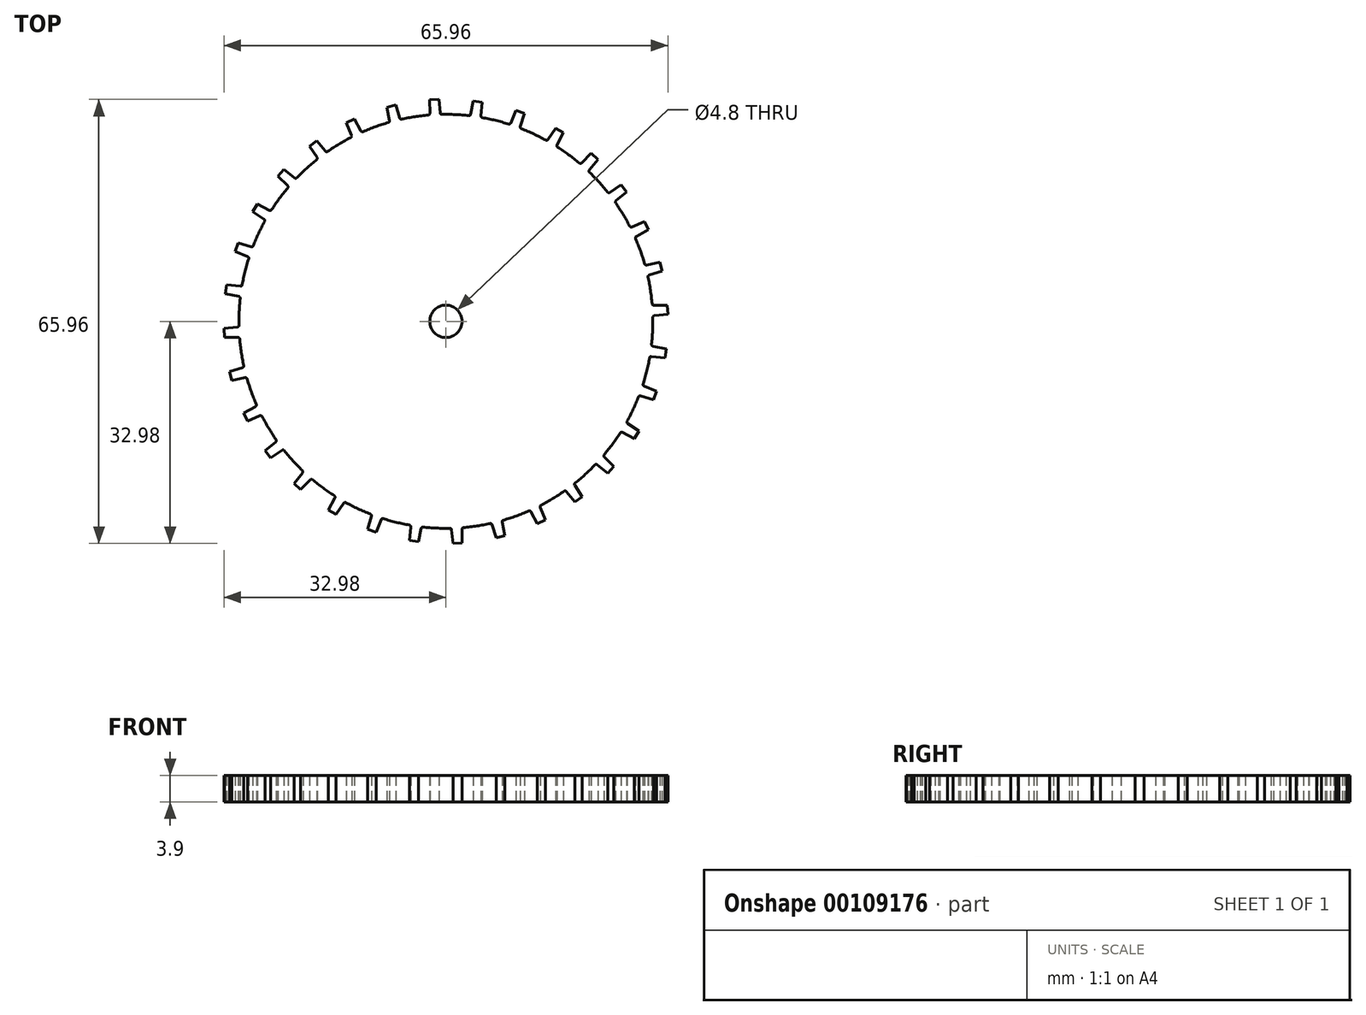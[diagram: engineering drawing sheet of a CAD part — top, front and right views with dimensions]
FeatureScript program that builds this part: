
annotation { "Feature Type Name" : "Feature", "Feature Type Description" : "" }
export const myFeature = defineFeature(function(context is Context, id is Id, definition is map)
    precondition{}
    {
        {
            var Q0;
            Q0=qCreatedBy(makeId("Top.planeOp"),FACE);
            var sketch = newSketch(context, id + "F0", { "sketchPlane" : qUnion([Q0])});
            skCircle(sketch, "E0", {"center": v(0, 0) * mm, "radius": 2.4 * mm});
            skCircle(sketch, "E1", {"center": v(0, 0) * mm, "radius": 32 * mm, "construction": true});
            skCircle(sketch, "E2", {"center": v(0, 0) * mm, "radius": 30.75 * mm});
            skCircle(sketch, "E3", {"center": v(0, 0) * mm, "radius": 31 * mm, "construction": true});
            skCircle(sketch, "E4", {"center": v(0, 0) * mm, "radius": 33 * mm, "construction": true});
            skLineSegment(sketch, "E5", {"start": v(3.64, 30.53) * mm, "end": v(4.08, 32.75) * mm});
            skLineSegment(sketch, "E6", {"start": v(5.4, 32.55) * mm, "end": v(5.2, 30.3) * mm});
            skLineSegment(sketch, "E7", {"start": v(4.08, 32.75) * mm, "end": v(5.4, 32.55) * mm});
            skLineSegment(sketch, "E8.1.0", {"start": v(10.39, 31.32) * mm, "end": v(11.65, 30.87) * mm});
            skLineSegment(sketch, "E8.1.1", {"start": v(11.65, 30.87) * mm, "end": v(11, 28.71) * mm});
            skLineSegment(sketch, "E8.1.2", {"start": v(9.53, 29.24) * mm, "end": v(10.39, 31.32) * mm});
            skLineSegment(sketch, "E8.2.0", {"start": v(16.3, 28.7) * mm, "end": v(17.45, 28) * mm});
            skLineSegment(sketch, "E8.2.1", {"start": v(17.45, 28) * mm, "end": v(16.4, 26.02) * mm});
            skLineSegment(sketch, "E8.2.2", {"start": v(15.05, 26.82) * mm, "end": v(16.3, 28.7) * mm});
            skLineSegment(sketch, "E8.3.0", {"start": v(21.58, 24.96) * mm, "end": v(22.58, 24.07) * mm});
            skLineSegment(sketch, "E8.3.1", {"start": v(22.58, 24.07) * mm, "end": v(21.15, 22.32) * mm});
            skLineSegment(sketch, "E8.3.2", {"start": v(20, 23.36) * mm, "end": v(21.58, 24.96) * mm});
            skLineSegment(sketch, "E8.4.0", {"start": v(26.04, 20.27) * mm, "end": v(26.84, 19.2) * mm});
            skLineSegment(sketch, "E8.4.1", {"start": v(26.84, 19.2) * mm, "end": v(25.1, 17.76) * mm});
            skLineSegment(sketch, "E8.4.2", {"start": v(24.17, 19.02) * mm, "end": v(26.04, 20.27) * mm});
            skLineSegment(sketch, "E8.5.0", {"start": v(29.5, 14.8) * mm, "end": v(30.07, 13.6) * mm});
            skLineSegment(sketch, "E8.5.1", {"start": v(30.07, 13.6) * mm, "end": v(28.08, 12.52) * mm});
            skLineSegment(sketch, "E8.5.2", {"start": v(27.41, 13.94) * mm, "end": v(29.5, 14.8) * mm});
            skLineSegment(sketch, "E8.6.0", {"start": v(31.81, 8.77) * mm, "end": v(32.14, 7.46) * mm});
            skLineSegment(sketch, "E8.6.1", {"start": v(32.14, 7.46) * mm, "end": v(29.99, 6.8) * mm});
            skLineSegment(sketch, "E8.6.2", {"start": v(29.6, 8.32) * mm, "end": v(31.81, 8.77) * mm});
            skLineSegment(sketch, "E8.7.0", {"start": v(32.91, 2.4) * mm, "end": v(32.98, 1.05) * mm});
            skLineSegment(sketch, "E8.7.1", {"start": v(32.98, 1.05) * mm, "end": v(30.74, 0.82) * mm});
            skLineSegment(sketch, "E8.7.2", {"start": v(30.66, 2.38) * mm, "end": v(32.91, 2.4) * mm});
            skLineSegment(sketch, "E8.8.0", {"start": v(32.75, -4.08) * mm, "end": v(32.55, -5.4) * mm});
            skLineSegment(sketch, "E8.8.1", {"start": v(32.55, -5.4) * mm, "end": v(30.3, -5.2) * mm});
            skLineSegment(sketch, "E8.8.2", {"start": v(30.53, -3.64) * mm, "end": v(32.75, -4.08) * mm});
            skLineSegment(sketch, "E8.9.0", {"start": v(31.32, -10.39) * mm, "end": v(30.87, -11.65) * mm});
            skLineSegment(sketch, "E8.9.1", {"start": v(30.87, -11.65) * mm, "end": v(28.71, -11) * mm});
            skLineSegment(sketch, "E8.9.2", {"start": v(29.24, -9.53) * mm, "end": v(31.32, -10.39) * mm});
            skLineSegment(sketch, "E8.10.0", {"start": v(28.7, -16.3) * mm, "end": v(28, -17.45) * mm});
            skLineSegment(sketch, "E8.10.1", {"start": v(28, -17.45) * mm, "end": v(26.02, -16.4) * mm});
            skLineSegment(sketch, "E8.10.2", {"start": v(26.82, -15.05) * mm, "end": v(28.7, -16.3) * mm});
            skLineSegment(sketch, "E8.11.0", {"start": v(24.96, -21.58) * mm, "end": v(24.07, -22.58) * mm});
            skLineSegment(sketch, "E8.11.1", {"start": v(24.07, -22.58) * mm, "end": v(22.32, -21.15) * mm});
            skLineSegment(sketch, "E8.11.2", {"start": v(23.36, -20) * mm, "end": v(24.96, -21.58) * mm});
            skLineSegment(sketch, "E8.12.0", {"start": v(20.27, -26.04) * mm, "end": v(19.2, -26.84) * mm});
            skLineSegment(sketch, "E8.12.1", {"start": v(19.2, -26.84) * mm, "end": v(17.76, -25.1) * mm});
            skLineSegment(sketch, "E8.12.2", {"start": v(19.02, -24.17) * mm, "end": v(20.27, -26.04) * mm});
            skLineSegment(sketch, "E8.13.0", {"start": v(14.8, -29.5) * mm, "end": v(13.6, -30.07) * mm});
            skLineSegment(sketch, "E8.13.1", {"start": v(13.6, -30.07) * mm, "end": v(12.52, -28.08) * mm});
            skLineSegment(sketch, "E8.13.2", {"start": v(13.94, -27.41) * mm, "end": v(14.8, -29.5) * mm});
            skLineSegment(sketch, "E8.14.0", {"start": v(8.77, -31.81) * mm, "end": v(7.46, -32.14) * mm});
            skLineSegment(sketch, "E8.14.1", {"start": v(7.46, -32.14) * mm, "end": v(6.8, -29.99) * mm});
            skLineSegment(sketch, "E8.14.2", {"start": v(8.32, -29.6) * mm, "end": v(8.77, -31.81) * mm});
            skLineSegment(sketch, "E8.15.0", {"start": v(2.4, -32.91) * mm, "end": v(1.05, -32.98) * mm});
            skLineSegment(sketch, "E8.15.1", {"start": v(1.05, -32.98) * mm, "end": v(0.82, -30.74) * mm});
            skLineSegment(sketch, "E8.15.2", {"start": v(2.38, -30.66) * mm, "end": v(2.4, -32.91) * mm});
            skLineSegment(sketch, "E8.16.0", {"start": v(-4.08, -32.75) * mm, "end": v(-5.4, -32.55) * mm});
            skLineSegment(sketch, "E8.16.1", {"start": v(-5.4, -32.55) * mm, "end": v(-5.2, -30.3) * mm});
            skLineSegment(sketch, "E8.16.2", {"start": v(-3.64, -30.53) * mm, "end": v(-4.08, -32.75) * mm});
            skLineSegment(sketch, "E8.17.0", {"start": v(-10.39, -31.32) * mm, "end": v(-11.65, -30.87) * mm});
            skLineSegment(sketch, "E8.17.1", {"start": v(-11.65, -30.87) * mm, "end": v(-11, -28.71) * mm});
            skLineSegment(sketch, "E8.17.2", {"start": v(-9.53, -29.24) * mm, "end": v(-10.39, -31.32) * mm});
            skLineSegment(sketch, "E8.18.0", {"start": v(-16.3, -28.7) * mm, "end": v(-17.45, -28) * mm});
            skLineSegment(sketch, "E8.18.1", {"start": v(-17.45, -28) * mm, "end": v(-16.4, -26.02) * mm});
            skLineSegment(sketch, "E8.18.2", {"start": v(-15.05, -26.82) * mm, "end": v(-16.3, -28.7) * mm});
            skLineSegment(sketch, "E8.19.0", {"start": v(-21.58, -24.96) * mm, "end": v(-22.58, -24.07) * mm});
            skLineSegment(sketch, "E8.19.1", {"start": v(-22.58, -24.07) * mm, "end": v(-21.15, -22.32) * mm});
            skLineSegment(sketch, "E8.19.2", {"start": v(-20, -23.36) * mm, "end": v(-21.58, -24.96) * mm});
            skLineSegment(sketch, "E8.20.0", {"start": v(-26.04, -20.27) * mm, "end": v(-26.84, -19.2) * mm});
            skLineSegment(sketch, "E8.20.1", {"start": v(-26.84, -19.2) * mm, "end": v(-25.1, -17.76) * mm});
            skLineSegment(sketch, "E8.20.2", {"start": v(-24.17, -19.02) * mm, "end": v(-26.04, -20.27) * mm});
            skLineSegment(sketch, "E8.21.0", {"start": v(-29.5, -14.8) * mm, "end": v(-30.07, -13.6) * mm});
            skLineSegment(sketch, "E8.21.1", {"start": v(-30.07, -13.6) * mm, "end": v(-28.08, -12.52) * mm});
            skLineSegment(sketch, "E8.21.2", {"start": v(-27.41, -13.94) * mm, "end": v(-29.5, -14.8) * mm});
            skLineSegment(sketch, "E8.22.0", {"start": v(-31.81, -8.77) * mm, "end": v(-32.14, -7.46) * mm});
            skLineSegment(sketch, "E8.22.1", {"start": v(-32.14, -7.46) * mm, "end": v(-29.99, -6.8) * mm});
            skLineSegment(sketch, "E8.22.2", {"start": v(-29.6, -8.32) * mm, "end": v(-31.81, -8.77) * mm});
            skLineSegment(sketch, "E8.23.0", {"start": v(-32.91, -2.4) * mm, "end": v(-32.98, -1.05) * mm});
            skLineSegment(sketch, "E8.23.1", {"start": v(-32.98, -1.05) * mm, "end": v(-30.74, -0.82) * mm});
            skLineSegment(sketch, "E8.23.2", {"start": v(-30.66, -2.38) * mm, "end": v(-32.91, -2.4) * mm});
            skLineSegment(sketch, "E8.24.0", {"start": v(-32.75, 4.08) * mm, "end": v(-32.55, 5.4) * mm});
            skLineSegment(sketch, "E8.24.1", {"start": v(-32.55, 5.4) * mm, "end": v(-30.3, 5.2) * mm});
            skLineSegment(sketch, "E8.24.2", {"start": v(-30.53, 3.64) * mm, "end": v(-32.75, 4.08) * mm});
            skLineSegment(sketch, "E8.25.0", {"start": v(-31.32, 10.39) * mm, "end": v(-30.87, 11.65) * mm});
            skLineSegment(sketch, "E8.25.1", {"start": v(-30.87, 11.65) * mm, "end": v(-28.71, 11) * mm});
            skLineSegment(sketch, "E8.25.2", {"start": v(-29.24, 9.53) * mm, "end": v(-31.32, 10.39) * mm});
            skLineSegment(sketch, "E8.26.0", {"start": v(-28.7, 16.3) * mm, "end": v(-28, 17.45) * mm});
            skLineSegment(sketch, "E8.26.1", {"start": v(-28, 17.45) * mm, "end": v(-26.02, 16.4) * mm});
            skLineSegment(sketch, "E8.26.2", {"start": v(-26.82, 15.05) * mm, "end": v(-28.7, 16.3) * mm});
            skLineSegment(sketch, "E8.27.0", {"start": v(-24.96, 21.58) * mm, "end": v(-24.07, 22.58) * mm});
            skLineSegment(sketch, "E8.27.1", {"start": v(-24.07, 22.58) * mm, "end": v(-22.32, 21.15) * mm});
            skLineSegment(sketch, "E8.27.2", {"start": v(-23.36, 20) * mm, "end": v(-24.96, 21.58) * mm});
            skLineSegment(sketch, "E8.28.0", {"start": v(-20.27, 26.04) * mm, "end": v(-19.2, 26.84) * mm});
            skLineSegment(sketch, "E8.28.1", {"start": v(-19.2, 26.84) * mm, "end": v(-17.76, 25.1) * mm});
            skLineSegment(sketch, "E8.28.2", {"start": v(-19.02, 24.17) * mm, "end": v(-20.27, 26.04) * mm});
            skLineSegment(sketch, "E8.29.0", {"start": v(-14.8, 29.5) * mm, "end": v(-13.6, 30.07) * mm});
            skLineSegment(sketch, "E8.29.1", {"start": v(-13.6, 30.07) * mm, "end": v(-12.52, 28.08) * mm});
            skLineSegment(sketch, "E8.29.2", {"start": v(-13.94, 27.41) * mm, "end": v(-14.8, 29.5) * mm});
            skLineSegment(sketch, "E8.30.0", {"start": v(-8.77, 31.81) * mm, "end": v(-7.46, 32.14) * mm});
            skLineSegment(sketch, "E8.30.1", {"start": v(-7.46, 32.14) * mm, "end": v(-6.8, 29.99) * mm});
            skLineSegment(sketch, "E8.30.2", {"start": v(-8.32, 29.6) * mm, "end": v(-8.77, 31.81) * mm});
            skLineSegment(sketch, "E8.31.0", {"start": v(-2.4, 32.91) * mm, "end": v(-1.05, 32.98) * mm});
            skLineSegment(sketch, "E8.31.1", {"start": v(-1.05, 32.98) * mm, "end": v(-0.82, 30.74) * mm});
            skLineSegment(sketch, "E8.31.2", {"start": v(-2.38, 30.66) * mm, "end": v(-2.4, 32.91) * mm});
            skLineSegment(sketch, "E8.anchor1", {"start": v(0, 0) * mm, "end": v(4.08, 32.75) * mm, "construction": true});
            skLineSegment(sketch, "E8.anchor2", {"start": v(0, 0) * mm, "end": v(-2.4, 32.91) * mm, "construction": true});
            skSolve(sketch);
        }
        {
            var Q0;
            Q0=makeQuery(id+"F0.imprint","IMPRINT",FACE,{"disambiguationData":[TD([[makeQuery(id+"F0.imprint","IMPRINT",EDGE,{"derivedFrom":sQuery(id+"F0.wireOp",EDGE,"E8.14.0")}),-1.0]])]});
            var Q1;
            Q1=makeQuery(id+"F0.imprint","IMPRINT",FACE,{"disambiguationData":[TD([[makeQuery(id+"F0.imprint","IMPRINT",EDGE,{"derivedFrom":sQuery(id+"F0.wireOp",EDGE,"E8.11.0")}),-1.0]])]});
            var Q2;
            Q2=makeQuery(id+"F0.imprint","IMPRINT",FACE,{"disambiguationData":[TD([[makeQuery(id+"F0.imprint","IMPRINT",EDGE,{"derivedFrom":sQuery(id+"F0.wireOp",EDGE,"E8.13.0")}),-1.0]])]});
            var Q3;
            Q3=makeQuery(id+"F0.imprint","IMPRINT",FACE,{"disambiguationData":[TD([[makeQuery(id+"F0.imprint","IMPRINT",EDGE,{"derivedFrom":sQuery(id+"F0.wireOp",EDGE,"E8.10.0")}),-1.0]])]});
            var Q4;
            Q4=makeQuery(id+"F0.imprint","IMPRINT",FACE,{"disambiguationData":[TD([[makeQuery(id+"F0.imprint","IMPRINT",EDGE,{"derivedFrom":sQuery(id+"F0.wireOp",EDGE,"E8.12.0")}),-1.0]])]});
            var Q5;
            Q5=makeQuery(id+"F0.imprint","IMPRINT",FACE,{"disambiguationData":[TD([[makeQuery(id+"F0.imprint","IMPRINT",EDGE,{"derivedFrom":sQuery(id+"F0.wireOp",EDGE,"E8.18.0")}),-1.0]])]});
            var Q6;
            Q6=makeQuery(id+"F0.imprint","IMPRINT",FACE,{"disambiguationData":[TD([[makeQuery(id+"F0.imprint","IMPRINT",EDGE,{"derivedFrom":sQuery(id+"F0.wireOp",EDGE,"E8.8.0")}),-1.0]])]});
            var Q7;
            Q7=makeQuery(id+"F0.imprint","IMPRINT",FACE,{"disambiguationData":[TD([[makeQuery(id+"F0.imprint","IMPRINT",EDGE,{"derivedFrom":sQuery(id+"F0.wireOp",EDGE,"E8.7.0")}),-1.0]])]});
            var Q8;
            Q8=makeQuery(id+"F0.imprint","IMPRINT",FACE,{"disambiguationData":[TD([[makeQuery(id+"F0.imprint","IMPRINT",EDGE,{"derivedFrom":sQuery(id+"F0.wireOp",EDGE,"E8.6.0")}),-1.0]])]});
            var Q9;
            Q9=makeQuery(id+"F0.imprint","IMPRINT",FACE,{"disambiguationData":[TD([[makeQuery(id+"F0.imprint","IMPRINT",EDGE,{"derivedFrom":sQuery(id+"F0.wireOp",EDGE,"E8.5.0")}),-1.0]])]});
            var Q10;
            Q10=makeQuery(id+"F0.imprint","IMPRINT",FACE,{"disambiguationData":[TD([[makeQuery(id+"F0.imprint","IMPRINT",EDGE,{"derivedFrom":sQuery(id+"F0.wireOp",EDGE,"E8.4.0")}),-1.0]])]});
            var Q11;
            Q11=makeQuery(id+"F0.imprint","IMPRINT",FACE,{"disambiguationData":[TD([[makeQuery(id+"F0.imprint","IMPRINT",EDGE,{"derivedFrom":sQuery(id+"F0.wireOp",EDGE,"E8.3.0")}),-1.0]])]});
            var Q12;
            Q12=makeQuery(id+"F0.imprint","IMPRINT",FACE,{"disambiguationData":[TD([[makeQuery(id+"F0.imprint","IMPRINT",EDGE,{"derivedFrom":sQuery(id+"F0.wireOp",EDGE,"E8.2.0")}),-1.0]])]});
            var Q13;
            Q13=makeQuery(id+"F0.imprint","IMPRINT",FACE,{"disambiguationData":[TD([[makeQuery(id+"F0.imprint","IMPRINT",EDGE,{"derivedFrom":sQuery(id+"F0.wireOp",EDGE,"E8.1.0")}),-1.0]])]});
            var Q14;
            {var subQ0=sQuery(id+"F0.wireOp",EDGE,"E5");Q14=makeQuery(id+"F0.imprint","IMPRINT",FACE,{"disambiguationData":[TD([[makeQuery(id+"F0.imprint","IMPRINT",EDGE,{"derivedFrom":subQ0}),-1.0]])]});}
            var Q15;
            Q15=makeQuery(id+"F0.imprint","IMPRINT",FACE,{"disambiguationData":[TD([[makeQuery(id+"F0.imprint","IMPRINT",EDGE,{"derivedFrom":sQuery(id+"F0.wireOp",EDGE,"E8.31.0")}),-1.0]])]});
            var Q16;
            Q16=makeQuery(id+"F0.imprint","IMPRINT",FACE,{"disambiguationData":[TD([[makeQuery(id+"F0.imprint","IMPRINT",EDGE,{"derivedFrom":sQuery(id+"F0.wireOp",EDGE,"E8.30.0")}),-1.0]])]});
            var Q17;
            Q17=makeQuery(id+"F0.imprint","IMPRINT",FACE,{"disambiguationData":[TD([[makeQuery(id+"F0.imprint","IMPRINT",EDGE,{"derivedFrom":sQuery(id+"F0.wireOp",EDGE,"E8.29.0")}),-1.0]])]});
            var Q18;
            Q18=makeQuery(id+"F0.imprint","IMPRINT",FACE,{"disambiguationData":[TD([[makeQuery(id+"F0.imprint","IMPRINT",EDGE,{"derivedFrom":sQuery(id+"F0.wireOp",EDGE,"E8.17.0")}),-1.0]])]});
            var Q19;
            Q19=makeQuery(id+"F0.imprint","IMPRINT",FACE,{"disambiguationData":[TD([[makeQuery(id+"F0.imprint","IMPRINT",EDGE,{"derivedFrom":sQuery(id+"F0.wireOp",EDGE,"E8.16.0")}),-1.0]])]});
            var Q20;
            Q20=makeQuery(id+"F0.imprint","IMPRINT",FACE,{"disambiguationData":[TD([[makeQuery(id+"F0.imprint","IMPRINT",EDGE,{"derivedFrom":sQuery(id+"F0.wireOp",EDGE,"E8.9.0")}),-1.0]])]});
            var Q21;
            Q21=makeQuery(id+"F0.imprint","IMPRINT",FACE,{"disambiguationData":[TD([[makeQuery(id+"F0.imprint","IMPRINT",EDGE,{"derivedFrom":sQuery(id+"F0.wireOp",EDGE,"E8.15.0")}),-1.0]])]});
            var Q22;
            Q22=makeQuery(id+"F0.imprint","IMPRINT",FACE,{"disambiguationData":[TD([[makeQuery(id+"F0.imprint","IMPRINT",EDGE,{"derivedFrom":sQuery(id+"F0.wireOp",EDGE,"E0")}),-1.0]])]});
            var Q23;
            Q23=makeQuery(id+"F0.imprint","IMPRINT",FACE,{"disambiguationData":[TD([[makeQuery(id+"F0.imprint","IMPRINT",EDGE,{"derivedFrom":sQuery(id+"F0.wireOp",EDGE,"E8.21.0")}),-1.0]])]});
            var Q24;
            Q24=makeQuery(id+"F0.imprint","IMPRINT",FACE,{"disambiguationData":[TD([[makeQuery(id+"F0.imprint","IMPRINT",EDGE,{"derivedFrom":sQuery(id+"F0.wireOp",EDGE,"E8.20.0")}),-1.0]])]});
            var Q25;
            Q25=makeQuery(id+"F0.imprint","IMPRINT",FACE,{"disambiguationData":[TD([[makeQuery(id+"F0.imprint","IMPRINT",EDGE,{"derivedFrom":sQuery(id+"F0.wireOp",EDGE,"E8.25.0")}),-1.0]])]});
            var Q26;
            Q26=makeQuery(id+"F0.imprint","IMPRINT",FACE,{"disambiguationData":[TD([[makeQuery(id+"F0.imprint","IMPRINT",EDGE,{"derivedFrom":sQuery(id+"F0.wireOp",EDGE,"E8.27.0")}),-1.0]])]});
            var Q27;
            Q27=makeQuery(id+"F0.imprint","IMPRINT",FACE,{"disambiguationData":[TD([[makeQuery(id+"F0.imprint","IMPRINT",EDGE,{"derivedFrom":sQuery(id+"F0.wireOp",EDGE,"E8.24.0")}),-1.0]])]});
            var Q28;
            Q28=makeQuery(id+"F0.imprint","IMPRINT",FACE,{"disambiguationData":[TD([[makeQuery(id+"F0.imprint","IMPRINT",EDGE,{"derivedFrom":sQuery(id+"F0.wireOp",EDGE,"E8.26.0")}),-1.0]])]});
            var Q29;
            Q29=makeQuery(id+"F0.imprint","IMPRINT",FACE,{"disambiguationData":[TD([[makeQuery(id+"F0.imprint","IMPRINT",EDGE,{"derivedFrom":sQuery(id+"F0.wireOp",EDGE,"E8.23.0")}),-1.0]])]});
            var Q30;
            Q30=makeQuery(id+"F0.imprint","IMPRINT",FACE,{"disambiguationData":[TD([[makeQuery(id+"F0.imprint","IMPRINT",EDGE,{"derivedFrom":sQuery(id+"F0.wireOp",EDGE,"E8.22.0")}),-1.0]])]});
            var Q31;
            Q31=makeQuery(id+"F0.imprint","IMPRINT",FACE,{"disambiguationData":[TD([[makeQuery(id+"F0.imprint","IMPRINT",EDGE,{"derivedFrom":sQuery(id+"F0.wireOp",EDGE,"E8.19.0")}),-1.0]])]});
            var Q32;
            Q32=makeQuery(id+"F0.imprint","IMPRINT",FACE,{"disambiguationData":[TD([[makeQuery(id+"F0.imprint","IMPRINT",EDGE,{"derivedFrom":sQuery(id+"F0.wireOp",EDGE,"E8.28.0")}),-1.0]])]});
            extrude(context, id + "F1", {"entities" : qUnion([Q0, Q1, Q2, Q3, Q4, Q5, Q6, Q7, Q8, Q9, Q10, Q11, Q12, Q13, Q14, Q15, Q16, Q17, Q18, Q19, Q20, Q21, Q22, Q23, Q24, Q25, Q26, Q27, Q28, Q29, Q30, Q31, Q32]), "endBound" : BoundingType.SYMMETRIC, "depth" : 3.9 * mm});
        }
        {
            var Q0;
            Q0=makeQuery(id+"F1.opExtrude","SWEPT_EDGE",EDGE,{"disambiguationData":[OSD([sQuery(id+"F0.wireOp",EDGE,"E2"),sQuery(id+"F0.wireOp",EDGE,"E8.30.2")])]});
            var Q1;
            Q1=makeQuery(id+"F1.opExtrude","SWEPT_EDGE",EDGE,{"disambiguationData":[OSD([sQuery(id+"F0.wireOp",EDGE,"E2"),sQuery(id+"F0.wireOp",EDGE,"E8.30.1")])]});
            var Q2;
            Q2=makeQuery(id+"F1.opExtrude","SWEPT_EDGE",EDGE,{"disambiguationData":[OSD([sQuery(id+"F0.wireOp",EDGE,"E2"),sQuery(id+"F0.wireOp",EDGE,"E8.31.2")])]});
            var Q3;
            Q3=makeQuery(id+"F1.opExtrude","SWEPT_EDGE",EDGE,{"disambiguationData":[OSD([sQuery(id+"F0.wireOp",EDGE,"E2"),sQuery(id+"F0.wireOp",EDGE,"E5")])]});
            var Q4;
            Q4=makeQuery(id+"F1.opExtrude","SWEPT_EDGE",EDGE,{"disambiguationData":[OSD([sQuery(id+"F0.wireOp",EDGE,"E2"),sQuery(id+"F0.wireOp",EDGE,"E8.1.2")])]});
            var Q5;
            Q5=makeQuery(id+"F1.opExtrude","SWEPT_EDGE",EDGE,{"disambiguationData":[OSD([sQuery(id+"F0.wireOp",EDGE,"E2"),sQuery(id+"F0.wireOp",EDGE,"E8.2.2")])]});
            var Q6;
            Q6=makeQuery(id+"F1.opExtrude","SWEPT_EDGE",EDGE,{"disambiguationData":[OSD([sQuery(id+"F0.wireOp",EDGE,"E2"),sQuery(id+"F0.wireOp",EDGE,"E8.3.2")])]});
            var Q7;
            Q7=makeQuery(id+"F1.opExtrude","SWEPT_EDGE",EDGE,{"disambiguationData":[OSD([sQuery(id+"F0.wireOp",EDGE,"E2"),sQuery(id+"F0.wireOp",EDGE,"E8.4.2")])]});
            var Q8;
            Q8=makeQuery(id+"F1.opExtrude","SWEPT_EDGE",EDGE,{"disambiguationData":[OSD([sQuery(id+"F0.wireOp",EDGE,"E2"),sQuery(id+"F0.wireOp",EDGE,"E8.5.2")])]});
            var Q9;
            Q9=makeQuery(id+"F1.opExtrude","SWEPT_EDGE",EDGE,{"disambiguationData":[OSD([sQuery(id+"F0.wireOp",EDGE,"E2"),sQuery(id+"F0.wireOp",EDGE,"E8.6.2")])]});
            var Q10;
            Q10=makeQuery(id+"F1.opExtrude","SWEPT_EDGE",EDGE,{"disambiguationData":[OSD([sQuery(id+"F0.wireOp",EDGE,"E2"),sQuery(id+"F0.wireOp",EDGE,"E8.7.2")])]});
            var Q11;
            Q11=makeQuery(id+"F1.opExtrude","SWEPT_EDGE",EDGE,{"disambiguationData":[OSD([sQuery(id+"F0.wireOp",EDGE,"E2"),sQuery(id+"F0.wireOp",EDGE,"E8.8.2")])]});
            var Q12;
            Q12=makeQuery(id+"F1.opExtrude","SWEPT_EDGE",EDGE,{"disambiguationData":[OSD([sQuery(id+"F0.wireOp",EDGE,"E2"),sQuery(id+"F0.wireOp",EDGE,"E8.9.2")])]});
            var Q13;
            Q13=makeQuery(id+"F1.opExtrude","SWEPT_EDGE",EDGE,{"disambiguationData":[OSD([sQuery(id+"F0.wireOp",EDGE,"E2"),sQuery(id+"F0.wireOp",EDGE,"E8.10.2")])]});
            var Q14;
            Q14=makeQuery(id+"F1.opExtrude","SWEPT_EDGE",EDGE,{"disambiguationData":[OSD([sQuery(id+"F0.wireOp",EDGE,"E2"),sQuery(id+"F0.wireOp",EDGE,"E8.11.2")])]});
            var Q15;
            Q15=makeQuery(id+"F1.opExtrude","SWEPT_EDGE",EDGE,{"disambiguationData":[OSD([sQuery(id+"F0.wireOp",EDGE,"E2"),sQuery(id+"F0.wireOp",EDGE,"E8.12.2")])]});
            var Q16;
            Q16=makeQuery(id+"F1.opExtrude","SWEPT_EDGE",EDGE,{"disambiguationData":[OSD([sQuery(id+"F0.wireOp",EDGE,"E2"),sQuery(id+"F0.wireOp",EDGE,"E8.13.2")])]});
            var Q17;
            Q17=makeQuery(id+"F1.opExtrude","SWEPT_EDGE",EDGE,{"disambiguationData":[OSD([sQuery(id+"F0.wireOp",EDGE,"E2"),sQuery(id+"F0.wireOp",EDGE,"E8.14.2")])]});
            var Q18;
            Q18=makeQuery(id+"F1.opExtrude","SWEPT_EDGE",EDGE,{"disambiguationData":[OSD([sQuery(id+"F0.wireOp",EDGE,"E2"),sQuery(id+"F0.wireOp",EDGE,"E8.15.2")])]});
            var Q19;
            Q19=makeQuery(id+"F1.opExtrude","SWEPT_EDGE",EDGE,{"disambiguationData":[OSD([sQuery(id+"F0.wireOp",EDGE,"E2"),sQuery(id+"F0.wireOp",EDGE,"E8.16.2")])]});
            var Q20;
            Q20=makeQuery(id+"F1.opExtrude","SWEPT_EDGE",EDGE,{"disambiguationData":[OSD([sQuery(id+"F0.wireOp",EDGE,"E2"),sQuery(id+"F0.wireOp",EDGE,"E8.17.2")])]});
            var Q21;
            Q21=makeQuery(id+"F1.opExtrude","SWEPT_EDGE",EDGE,{"disambiguationData":[OSD([sQuery(id+"F0.wireOp",EDGE,"E2"),sQuery(id+"F0.wireOp",EDGE,"E8.18.2")])]});
            var Q22;
            Q22=makeQuery(id+"F1.opExtrude","SWEPT_EDGE",EDGE,{"disambiguationData":[OSD([sQuery(id+"F0.wireOp",EDGE,"E2"),sQuery(id+"F0.wireOp",EDGE,"E8.19.2")])]});
            var Q23;
            Q23=makeQuery(id+"F1.opExtrude","SWEPT_EDGE",EDGE,{"disambiguationData":[OSD([sQuery(id+"F0.wireOp",EDGE,"E2"),sQuery(id+"F0.wireOp",EDGE,"E8.20.2")])]});
            var Q24;
            Q24=makeQuery(id+"F1.opExtrude","SWEPT_EDGE",EDGE,{"disambiguationData":[OSD([sQuery(id+"F0.wireOp",EDGE,"E2"),sQuery(id+"F0.wireOp",EDGE,"E8.21.2")])]});
            var Q25;
            Q25=makeQuery(id+"F1.opExtrude","SWEPT_EDGE",EDGE,{"disambiguationData":[OSD([sQuery(id+"F0.wireOp",EDGE,"E2"),sQuery(id+"F0.wireOp",EDGE,"E8.22.2")])]});
            var Q26;
            Q26=makeQuery(id+"F1.opExtrude","SWEPT_EDGE",EDGE,{"disambiguationData":[OSD([sQuery(id+"F0.wireOp",EDGE,"E2"),sQuery(id+"F0.wireOp",EDGE,"E8.23.2")])]});
            var Q27;
            Q27=makeQuery(id+"F1.opExtrude","SWEPT_EDGE",EDGE,{"disambiguationData":[OSD([sQuery(id+"F0.wireOp",EDGE,"E2"),sQuery(id+"F0.wireOp",EDGE,"E8.24.2")])]});
            var Q28;
            Q28=makeQuery(id+"F1.opExtrude","SWEPT_EDGE",EDGE,{"disambiguationData":[OSD([sQuery(id+"F0.wireOp",EDGE,"E2"),sQuery(id+"F0.wireOp",EDGE,"E8.25.2")])]});
            var Q29;
            Q29=makeQuery(id+"F1.opExtrude","SWEPT_EDGE",EDGE,{"disambiguationData":[OSD([sQuery(id+"F0.wireOp",EDGE,"E2"),sQuery(id+"F0.wireOp",EDGE,"E8.26.2")])]});
            var Q30;
            Q30=makeQuery(id+"F1.opExtrude","SWEPT_EDGE",EDGE,{"disambiguationData":[OSD([sQuery(id+"F0.wireOp",EDGE,"E2"),sQuery(id+"F0.wireOp",EDGE,"E8.27.2")])]});
            var Q31;
            Q31=makeQuery(id+"F1.opExtrude","SWEPT_EDGE",EDGE,{"disambiguationData":[OSD([sQuery(id+"F0.wireOp",EDGE,"E2"),sQuery(id+"F0.wireOp",EDGE,"E8.28.2")])]});
            var Q32;
            Q32=makeQuery(id+"F1.opExtrude","SWEPT_EDGE",EDGE,{"disambiguationData":[OSD([sQuery(id+"F0.wireOp",EDGE,"E2"),sQuery(id+"F0.wireOp",EDGE,"E8.29.2")])]});
            var Q33;
            Q33=makeQuery(id+"F1.opExtrude","SWEPT_EDGE",EDGE,{"disambiguationData":[OSD([sQuery(id+"F0.wireOp",EDGE,"E2"),sQuery(id+"F0.wireOp",EDGE,"E8.26.1")])]});
            var Q34;
            Q34=makeQuery(id+"F1.opExtrude","SWEPT_EDGE",EDGE,{"disambiguationData":[OSD([sQuery(id+"F0.wireOp",EDGE,"E2"),sQuery(id+"F0.wireOp",EDGE,"E8.25.1")])]});
            var Q35;
            Q35=makeQuery(id+"F1.opExtrude","SWEPT_EDGE",EDGE,{"disambiguationData":[OSD([sQuery(id+"F0.wireOp",EDGE,"E2"),sQuery(id+"F0.wireOp",EDGE,"E8.24.1")])]});
            var Q36;
            Q36=makeQuery(id+"F1.opExtrude","SWEPT_EDGE",EDGE,{"disambiguationData":[OSD([sQuery(id+"F0.wireOp",EDGE,"E2"),sQuery(id+"F0.wireOp",EDGE,"E8.27.1")])]});
            var Q37;
            Q37=makeQuery(id+"F1.opExtrude","SWEPT_EDGE",EDGE,{"disambiguationData":[OSD([sQuery(id+"F0.wireOp",EDGE,"E2"),sQuery(id+"F0.wireOp",EDGE,"E8.28.1")])]});
            var Q38;
            Q38=makeQuery(id+"F1.opExtrude","SWEPT_EDGE",EDGE,{"disambiguationData":[OSD([sQuery(id+"F0.wireOp",EDGE,"E2"),sQuery(id+"F0.wireOp",EDGE,"E8.29.1")])]});
            var Q39;
            Q39=makeQuery(id+"F1.opExtrude","SWEPT_EDGE",EDGE,{"disambiguationData":[OSD([sQuery(id+"F0.wireOp",EDGE,"E2"),sQuery(id+"F0.wireOp",EDGE,"E8.31.1")])]});
            var Q40;
            Q40=makeQuery(id+"F1.opExtrude","SWEPT_EDGE",EDGE,{"disambiguationData":[OSD([sQuery(id+"F0.wireOp",EDGE,"E2"),sQuery(id+"F0.wireOp",EDGE,"E6")])]});
            var Q41;
            Q41=makeQuery(id+"F1.opExtrude","SWEPT_EDGE",EDGE,{"disambiguationData":[OSD([sQuery(id+"F0.wireOp",EDGE,"E2"),sQuery(id+"F0.wireOp",EDGE,"E8.1.1")])]});
            var Q42;
            Q42=makeQuery(id+"F1.opExtrude","SWEPT_EDGE",EDGE,{"disambiguationData":[OSD([sQuery(id+"F0.wireOp",EDGE,"E2"),sQuery(id+"F0.wireOp",EDGE,"E8.2.1")])]});
            var Q43;
            Q43=makeQuery(id+"F1.opExtrude","SWEPT_EDGE",EDGE,{"disambiguationData":[OSD([sQuery(id+"F0.wireOp",EDGE,"E2"),sQuery(id+"F0.wireOp",EDGE,"E8.3.1")])]});
            var Q44;
            Q44=makeQuery(id+"F1.opExtrude","SWEPT_EDGE",EDGE,{"disambiguationData":[OSD([sQuery(id+"F0.wireOp",EDGE,"E2"),sQuery(id+"F0.wireOp",EDGE,"E8.4.1")])]});
            var Q45;
            Q45=makeQuery(id+"F1.opExtrude","SWEPT_EDGE",EDGE,{"disambiguationData":[OSD([sQuery(id+"F0.wireOp",EDGE,"E2"),sQuery(id+"F0.wireOp",EDGE,"E8.5.1")])]});
            var Q46;
            Q46=makeQuery(id+"F1.opExtrude","SWEPT_EDGE",EDGE,{"disambiguationData":[OSD([sQuery(id+"F0.wireOp",EDGE,"E2"),sQuery(id+"F0.wireOp",EDGE,"E8.6.1")])]});
            var Q47;
            Q47=makeQuery(id+"F1.opExtrude","SWEPT_EDGE",EDGE,{"disambiguationData":[OSD([sQuery(id+"F0.wireOp",EDGE,"E2"),sQuery(id+"F0.wireOp",EDGE,"E8.7.1")])]});
            var Q48;
            Q48=makeQuery(id+"F1.opExtrude","SWEPT_EDGE",EDGE,{"disambiguationData":[OSD([sQuery(id+"F0.wireOp",EDGE,"E2"),sQuery(id+"F0.wireOp",EDGE,"E8.8.1")])]});
            var Q49;
            Q49=makeQuery(id+"F1.opExtrude","SWEPT_EDGE",EDGE,{"disambiguationData":[OSD([sQuery(id+"F0.wireOp",EDGE,"E2"),sQuery(id+"F0.wireOp",EDGE,"E8.9.1")])]});
            var Q50;
            Q50=makeQuery(id+"F1.opExtrude","SWEPT_EDGE",EDGE,{"disambiguationData":[OSD([sQuery(id+"F0.wireOp",EDGE,"E2"),sQuery(id+"F0.wireOp",EDGE,"E8.10.1")])]});
            fillet(context, id + "F2", {"entities" : qUnion([Q0, Q1, Q2, Q3, Q4, Q5, Q6, Q7, Q8, Q9, Q10, Q11, Q12, Q13, Q14, Q15, Q16, Q17, Q18, Q19, Q20, Q21, Q22, Q23, Q24, Q25, Q26, Q27, Q28, Q29, Q30, Q31, Q32, Q33, Q34, Q35, Q36, Q37, Q38, Q39, Q40, Q41, Q42, Q43, Q44, Q45, Q46, Q47, Q48, Q49, Q50]), "radius" : 0.25 * mm, "tangentPropagation" : true, "allowEdgeOverflow" : false});
        }
        {
            var Q0;
            Q0=makeQuery(id+"F1.opExtrude","SWEPT_EDGE",EDGE,{"disambiguationData":[OSD([sQuery(id+"F0.wireOp",EDGE,"E2"),sQuery(id+"F0.wireOp",EDGE,"E8.12.1")])]});
            var Q1;
            Q1=makeQuery(id+"F1.opExtrude","SWEPT_EDGE",EDGE,{"disambiguationData":[OSD([sQuery(id+"F0.wireOp",EDGE,"E2"),sQuery(id+"F0.wireOp",EDGE,"E8.11.1")])]});
            fillet(context, id + "F3", {"entities" : qUnion([Q0, Q1]), "radius" : 0.25 * mm, "tangentPropagation" : true, "allowEdgeOverflow" : false});
        }
        {
            var Q0;
            Q0=makeQuery(id+"F1.opExtrude","SWEPT_EDGE",EDGE,{"disambiguationData":[OSD([sQuery(id+"F0.wireOp",EDGE,"E2"),sQuery(id+"F0.wireOp",EDGE,"E8.13.1")])]});
            var Q1;
            Q1=makeQuery(id+"F1.opExtrude","SWEPT_EDGE",EDGE,{"disambiguationData":[OSD([sQuery(id+"F0.wireOp",EDGE,"E2"),sQuery(id+"F0.wireOp",EDGE,"E8.14.1")])]});
            var Q2;
            Q2=makeQuery(id+"F1.opExtrude","SWEPT_EDGE",EDGE,{"disambiguationData":[OSD([sQuery(id+"F0.wireOp",EDGE,"E2"),sQuery(id+"F0.wireOp",EDGE,"E8.15.1")])]});
            var Q3;
            Q3=makeQuery(id+"F1.opExtrude","SWEPT_EDGE",EDGE,{"disambiguationData":[OSD([sQuery(id+"F0.wireOp",EDGE,"E2"),sQuery(id+"F0.wireOp",EDGE,"E8.16.1")])]});
            var Q4;
            Q4=makeQuery(id+"F1.opExtrude","SWEPT_EDGE",EDGE,{"disambiguationData":[OSD([sQuery(id+"F0.wireOp",EDGE,"E2"),sQuery(id+"F0.wireOp",EDGE,"E8.17.1")])]});
            var Q5;
            Q5=makeQuery(id+"F1.opExtrude","SWEPT_EDGE",EDGE,{"disambiguationData":[OSD([sQuery(id+"F0.wireOp",EDGE,"E2"),sQuery(id+"F0.wireOp",EDGE,"E8.18.1")])]});
            var Q6;
            Q6=makeQuery(id+"F1.opExtrude","SWEPT_EDGE",EDGE,{"disambiguationData":[OSD([sQuery(id+"F0.wireOp",EDGE,"E2"),sQuery(id+"F0.wireOp",EDGE,"E8.19.1")])]});
            var Q7;
            Q7=makeQuery(id+"F1.opExtrude","SWEPT_EDGE",EDGE,{"disambiguationData":[OSD([sQuery(id+"F0.wireOp",EDGE,"E2"),sQuery(id+"F0.wireOp",EDGE,"E8.20.1")])]});
            var Q8;
            Q8=makeQuery(id+"F1.opExtrude","SWEPT_EDGE",EDGE,{"disambiguationData":[OSD([sQuery(id+"F0.wireOp",EDGE,"E2"),sQuery(id+"F0.wireOp",EDGE,"E8.21.1")])]});
            var Q9;
            Q9=makeQuery(id+"F1.opExtrude","SWEPT_EDGE",EDGE,{"disambiguationData":[OSD([sQuery(id+"F0.wireOp",EDGE,"E2"),sQuery(id+"F0.wireOp",EDGE,"E8.22.1")])]});
            fillet(context, id + "F4", {"entities" : qUnion([Q0, Q1, Q2, Q3, Q4, Q5, Q6, Q7, Q8, Q9]), "radius" : 0.25 * mm, "tangentPropagation" : true, "allowEdgeOverflow" : false});
        }
        {
            var Q0;
            Q0=makeQuery(id+"F1.opExtrude","SWEPT_EDGE",EDGE,{"disambiguationData":[OSD([sQuery(id+"F0.wireOp",EDGE,"E2"),sQuery(id+"F0.wireOp",EDGE,"E8.23.1")])]});
            fillet(context, id + "F5", {"entities" : qUnion([Q0]), "radius" : 0.25 * mm, "tangentPropagation" : true, "allowEdgeOverflow" : false});
        }
    });
